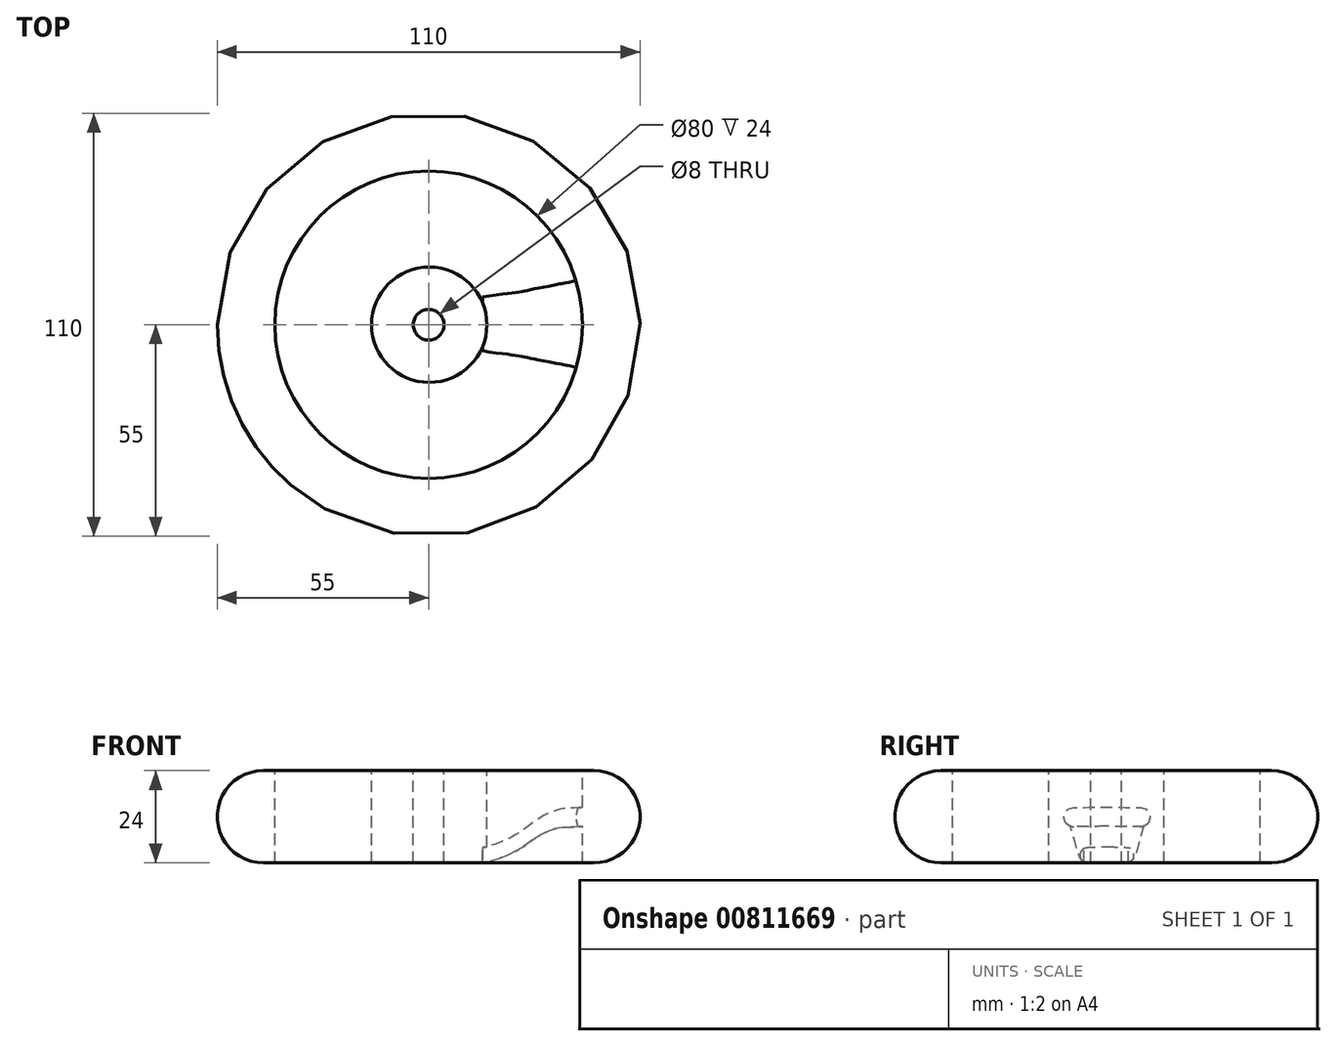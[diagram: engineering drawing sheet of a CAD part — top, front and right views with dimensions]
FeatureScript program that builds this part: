
annotation { "Feature Type Name" : "Feature", "Feature Type Description" : "" }
export const myFeature = defineFeature(function(context is Context, id is Id, definition is map)
    precondition{}
    {
        {
            var Q0;
            Q0=qCreatedBy(makeId("Top.planeOp"),FACE);
            var sketch = newSketch(context, id + "F0", { "sketchPlane" : qUnion([Q0])});
            skCircle(sketch, "E0", {"center": v(0, 0) * mm, "radius": 40 * mm});
            skSolve(sketch);
        }
        {
            var Q0;
            Q0=qCreatedBy(makeId("Front.planeOp"),FACE);
            var sketch = newSketch(context, id + "F1", { "sketchPlane" : qUnion([Q0])});
            skArc(sketch, "E1", {"start": v(-43, 12) * mm, "mid": v(-55, 0) * mm, "end": v(-43, -12) * mm});
            skLineSegment(sketch, "E2", {"start": v(-43, 12) * mm, "end": v(-40, 12) * mm});
            skLineSegment(sketch, "E3", {"start": v(-43, -12) * mm, "end": v(-40, -12) * mm});
            skLineSegment(sketch, "E4", {"start": v(-40, -12) * mm, "end": v(-40, 12) * mm});
            skSolve(sketch);
        }
        {
            var Q0;
            Q0 = qSketchRegion(id + "F1", true);
            var Q1;
            Q1 = qConstructionFilter(qBodyType(qCreatedBy(id + "F0" ,EDGE), BodyType.WIRE), ConstructionObject.NO);
            sweep(context, id + "F2", {"profiles" : qUnion([Q0]), "path" : qUnion([Q1])});
        }
        {
            var Q0;
            Q0=qCreatedBy(makeId("Right.planeOp"),FACE);
            cPlane(context, id + "F3", {"entities" : qUnion([Q0]), "cplaneType" : CPlaneType.OFFSET, "offset" : 40 * mm, "width" : 150 * mm, "height" : 150 * mm});
        }
        {
            var Q0;
            Q0=qCreatedBy(id+"F3.planeOp",FACE);
            var sketch = newSketch(context, id + "F4", { "sketchPlane" : qUnion([Q0])});
            skLineSegment(sketch, "E5", {"start": v(-8.8, 0) * mm, "end": v(9.2, 0) * mm});
            skArc(sketch, "E6.0.startCap", {"start": v(-8.8, -2.5) * mm, "mid": v(-11.3, 0) * mm, "end": v(-8.8, 2.5) * mm});
            skArc(sketch, "E6.0.endCap", {"start": v(9.2, 2.5) * mm, "mid": v(11.7, 0) * mm, "end": v(9.2, -2.5) * mm});
            skLineSegment(sketch, "E6.0.left", {"start": v(-8.8, 2.5) * mm, "end": v(9.2, 2.5) * mm});
            skLineSegment(sketch, "E6.0.right", {"start": v(-8.8, -2.5) * mm, "end": v(9.2, -2.5) * mm});
            skSolve(sketch);
        }
        {
            var Q0;
            Q0=qCreatedBy(makeId("Right.planeOp"),FACE);
            cPlane(context, id + "F5", {"entities" : qUnion([Q0]), "cplaneType" : CPlaneType.OFFSET, "offset" : 14 * mm, "width" : 150 * mm, "height" : 150 * mm});
        }
        {
            var Q0;
            Q0=qCreatedBy(id+"F5.planeOp",FACE);
            var sketch = newSketch(context, id + "F6", { "sketchPlane" : qUnion([Q0])});
            skLineSegment(sketch, "E7", {"start": v(-4.8, -10) * mm, "end": v(5.2, -10) * mm});
            skArc(sketch, "E8.0.startCap", {"start": v(-4.8, -12) * mm, "mid": v(-6.8, -10) * mm, "end": v(-4.8, -8) * mm});
            skArc(sketch, "E8.0.endCap", {"start": v(5.2, -8) * mm, "mid": v(7.2, -10) * mm, "end": v(5.2, -12) * mm});
            skLineSegment(sketch, "E8.0.left", {"start": v(-4.8, -8) * mm, "end": v(5.2, -8) * mm});
            skLineSegment(sketch, "E8.0.right", {"start": v(-4.8, -12) * mm, "end": v(5.2, -12) * mm});
            skSolve(sketch);
        }
        {
            var Q0;
            Q0=qCreatedBy(makeId("Front.planeOp"),FACE);
            var sketch = newSketch(context, id + "F7", { "sketchPlane" : qUnion([Q0])});
            skFitSpline(sketch, "E9", {"points": [v(14, -12) * mm, v(22.5, -9.03) * mm, v(27.25, -5.88) * mm, v(31.69, -3.53) * mm, v(35.32, -2.73) * mm, v(40, -2.5) * mm], "startDerivative": vector(22.08, 0.33) * mm, "endDerivative": vector(25.62, 4.02) * mm});
            skSolve(sketch);
        }
        {
            var Q1;
            Q1 = qSketchRegion(id + "F4", true);
            var Q2;
            Q2 = qSketchRegion(id + "F6", true);
            var Q3;
            Q3 = qConstructionFilter(qBodyType(qCreatedBy(id + "F7" ,EDGE), BodyType.WIRE), ConstructionObject.NO);
            loft(context, id + "F8", {"operationType" : NewBodyOperationType.ADD, "addGuides" : true, "sheetProfilesArray" : [{ "sheetProfileEntities" : qUnion([Q1]) }, { "sheetProfileEntities" : qUnion([Q2]) }], "guidesArray" : [{ "guideEntities" : qUnion([Q3]), "guideDerivativeType" : LoftGuideDerivativeType.DEFAULT, "guideDerivativeMagnitude" : 1 }]});
        }
        {
            var Q0;
            Q0=qCreatedBy(makeId("Front.planeOp"),FACE);
            var sketch = newSketch(context, id + "F9", { "sketchPlane" : qUnion([Q0])});
            skLineSegment(sketch, "E10.bottom", {"start": v(0.16, 12) * mm, "end": v(15.16, 12) * mm});
            skLineSegment(sketch, "E10.top", {"start": v(0.16, -12) * mm, "end": v(15.16, -12) * mm});
            skLineSegment(sketch, "E10.left", {"start": v(0.16, 12) * mm, "end": v(0.16, -12) * mm});
            skLineSegment(sketch, "E10.right", {"start": v(15.16, 12) * mm, "end": v(15.16, -12) * mm});
            skSolve(sketch);
        }
        {
            var Q0;
            Q0 = qSketchRegion(id + "F9", true);
            var Q1;
            Q1=sQuery(id+"F9.wireOp",EDGE,"E10.left");
            revolve(context, id + "F10", {"operationType" : NewBodyOperationType.ADD, "surfaceOperationType" : NewSurfaceOperationType.NEW, "entities" : qUnion([Q0]), "axis" : qUnion([Q1]), "revolveType" : RevolveType.FULL});
        }
        {
            var Q0;
            Q0=makeQuery(id+"F10.opRevolve","SWEPT_FACE",FACE,{"disambiguationData":[OSD([sQuery(id+"F9.wireOp",EDGE,"E10.bottom")])]});
            var sketch = newSketch(context, id + "F11", { "sketchPlane" : qUnion([Q0])});
            skPoint(sketch, "E11", {"position": v(0, 0) * mm});
            skSolve(sketch);
        }
        {
            var Q0;
            Q0=sQuery(id+"F11.wireOp",VERTEX,"E11");
            var Q1;
            Q1=makeQuery(id+"F2.opSweep","SWEPT_BODY",BODY,{"disambiguationData":[OSD([sQuery(id+"F0.wireOp",EDGE,"E0"),sQuery(id+"F1.wireOp",EDGE,"E1"),sQuery(id+"F1.wireOp",EDGE,"E2"),sQuery(id+"F1.wireOp",EDGE,"E3"),sQuery(id+"F1.wireOp",EDGE,"E4")])]});
            hole(context, id + "F12", {"style" : HoleStyle.SIMPLE, "endStyle" : HoleEndStyle.THROUGH, "holeDiameter" : 8 * mm, "majorDiameter" : 5 * mm, "isTappedThrough" : true, "tappedDepth" : 12 * mm, "tapClearance" : 3, "locations" : qUnion([Q0]), "scope" : qUnion([Q1])});
        }
    });
